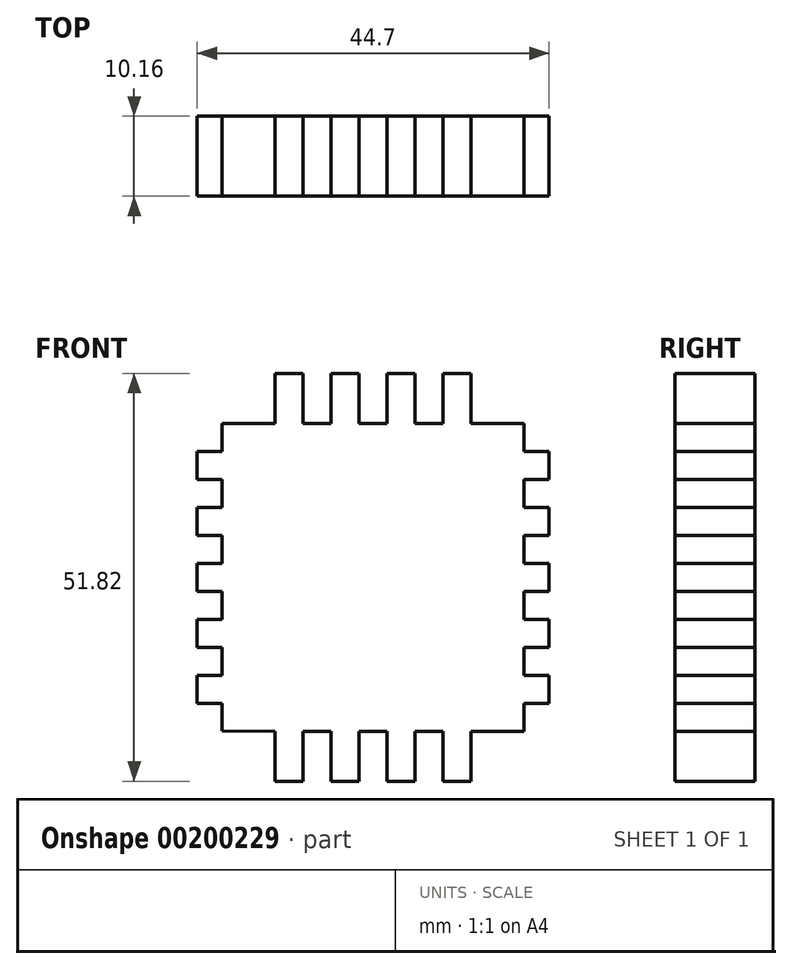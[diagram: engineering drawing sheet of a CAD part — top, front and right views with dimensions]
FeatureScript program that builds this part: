
annotation { "Feature Type Name" : "Feature", "Feature Type Description" : "" }
export const myFeature = defineFeature(function(context is Context, id is Id, definition is map)
    precondition{}
    {
        {
            var Q0;
            Q0=qCreatedBy(makeId("Front.planeOp"),FACE);
            var sketch = newSketch(context, id + "F0", { "sketchPlane" : qUnion([Q0])});
            skLineSegment(sketch, "E0", {"start": v(-12.15, -20.04) * mm, "end": v(-12.15, -26.39) * mm});
            skLineSegment(sketch, "E1", {"start": v(-12.15, -26.39) * mm, "end": v(-8.6, -26.39) * mm});
            skLineSegment(sketch, "E2", {"start": v(-8.6, -26.39) * mm, "end": v(-8.6, -20.04) * mm});
            skLineSegment(sketch, "E3", {"start": v(-8.6, -20.04) * mm, "end": v(-5.04, -20.04) * mm});
            skLineSegment(sketch, "E4", {"start": v(-5.04, -20.04) * mm, "end": v(-5.04, -26.39) * mm});
            skLineSegment(sketch, "E5", {"start": v(-5.04, -26.39) * mm, "end": v(-1.49, -26.39) * mm});
            skLineSegment(sketch, "E6", {"start": v(-1.49, -26.39) * mm, "end": v(-1.49, -20.04) * mm});
            skLineSegment(sketch, "E7", {"start": v(-1.49, -20.04) * mm, "end": v(2.07, -20.04) * mm});
            skLineSegment(sketch, "E8", {"start": v(2.07, -20.04) * mm, "end": v(2.07, -26.39) * mm});
            skLineSegment(sketch, "E9", {"start": v(2.07, -26.39) * mm, "end": v(5.63, -26.39) * mm});
            skLineSegment(sketch, "E10", {"start": v(5.63, -26.39) * mm, "end": v(5.63, -20.04) * mm});
            skLineSegment(sketch, "E11", {"start": v(5.63, -20.04) * mm, "end": v(9.18, -20.04) * mm});
            skLineSegment(sketch, "E12", {"start": v(9.18, -20.04) * mm, "end": v(9.18, -26.39) * mm});
            skLineSegment(sketch, "E13", {"start": v(9.18, -26.39) * mm, "end": v(12.74, -26.39) * mm});
            skLineSegment(sketch, "E14", {"start": v(12.74, -26.39) * mm, "end": v(12.74, -20.04) * mm});
            skLineSegment(sketch, "E15", {"start": v(22.64, -16.48) * mm, "end": v(22.64, -12.93) * mm});
            skLineSegment(sketch, "E16", {"start": v(22.64, -9.37) * mm, "end": v(22.64, -5.82) * mm});
            skLineSegment(sketch, "E17", {"start": v(22.64, -2.26) * mm, "end": v(22.64, 1.3) * mm});
            skLineSegment(sketch, "E18", {"start": v(22.64, 4.85) * mm, "end": v(22.64, 8.4) * mm});
            skLineSegment(sketch, "E19", {"start": v(22.64, 11.96) * mm, "end": v(22.64, 15.52) * mm});
            skLineSegment(sketch, "E20", {"start": v(12.74, 19.08) * mm, "end": v(12.74, 25.43) * mm});
            skLineSegment(sketch, "E21", {"start": v(12.74, 25.43) * mm, "end": v(9.18, 25.43) * mm});
            skLineSegment(sketch, "E22", {"start": v(9.18, 25.43) * mm, "end": v(9.18, 19.08) * mm});
            skLineSegment(sketch, "E23", {"start": v(9.18, 19.08) * mm, "end": v(5.63, 19.08) * mm});
            skLineSegment(sketch, "E24", {"start": v(5.63, 19.08) * mm, "end": v(5.63, 25.43) * mm});
            skLineSegment(sketch, "E25", {"start": v(5.63, 25.43) * mm, "end": v(2.07, 25.43) * mm});
            skLineSegment(sketch, "E26", {"start": v(2.07, 25.43) * mm, "end": v(2.07, 19.08) * mm});
            skLineSegment(sketch, "E27", {"start": v(2.07, 19.08) * mm, "end": v(-1.49, 19.08) * mm});
            skLineSegment(sketch, "E28", {"start": v(-1.49, 19.08) * mm, "end": v(-1.49, 25.43) * mm});
            skLineSegment(sketch, "E29", {"start": v(-1.49, 25.43) * mm, "end": v(-5.04, 25.43) * mm});
            skLineSegment(sketch, "E30", {"start": v(-5.04, 25.43) * mm, "end": v(-5.04, 19.08) * mm});
            skLineSegment(sketch, "E31", {"start": v(-5.04, 19.08) * mm, "end": v(-8.6, 19.08) * mm});
            skLineSegment(sketch, "E32", {"start": v(-8.6, 19.08) * mm, "end": v(-8.6, 25.43) * mm});
            skLineSegment(sketch, "E33", {"start": v(-8.6, 25.43) * mm, "end": v(-12.15, 25.43) * mm});
            skLineSegment(sketch, "E34", {"start": v(-12.15, 25.43) * mm, "end": v(-12.15, 19.08) * mm});
            skLineSegment(sketch, "E35", {"start": v(-22.06, -16.48) * mm, "end": v(-22.06, -12.93) * mm});
            skLineSegment(sketch, "E36", {"start": v(-22.06, -9.37) * mm, "end": v(-22.06, -5.82) * mm});
            skLineSegment(sketch, "E37", {"start": v(-22.06, -2.26) * mm, "end": v(-22.06, 1.3) * mm});
            skLineSegment(sketch, "E38", {"start": v(-22.06, 4.85) * mm, "end": v(-22.06, 8.4) * mm});
            skLineSegment(sketch, "E39", {"start": v(-22.06, 11.96) * mm, "end": v(-22.06, 15.52) * mm});
            skPoint(sketch, "E40.firstSnap0", {"position": v(-18.89, 15.52) * mm});
            skPoint(sketch, "E41.oppositeSnap0", {"position": v(19.47, -12.93) * mm});
            skLineSegment(sketch, "E42", {"start": v(22.64, 15.52) * mm, "end": v(19.47, 15.52) * mm});
            skLineSegment(sketch, "E43", {"start": v(22.64, 11.96) * mm, "end": v(19.47, 11.96) * mm});
            skLineSegment(sketch, "E44", {"start": v(22.64, 8.4) * mm, "end": v(19.47, 8.4) * mm});
            skLineSegment(sketch, "E45", {"start": v(22.64, 4.85) * mm, "end": v(19.47, 4.85) * mm});
            skLineSegment(sketch, "E46", {"start": v(22.64, -16.48) * mm, "end": v(19.47, -16.48) * mm});
            skLineSegment(sketch, "E47", {"start": v(22.64, -12.93) * mm, "end": v(19.47, -12.93) * mm});
            skLineSegment(sketch, "E48", {"start": v(22.64, -9.37) * mm, "end": v(19.47, -9.37) * mm});
            skLineSegment(sketch, "E49", {"start": v(22.64, -5.82) * mm, "end": v(19.47, -5.82) * mm});
            skLineSegment(sketch, "E50", {"start": v(22.64, -2.26) * mm, "end": v(19.47, -2.26) * mm});
            skLineSegment(sketch, "E51", {"start": v(22.64, 1.3) * mm, "end": v(19.47, 1.3) * mm});
            skLineSegment(sketch, "E52", {"start": v(19.47, 19.08) * mm, "end": v(19.47, 15.52) * mm});
            skLineSegment(sketch, "E53", {"start": v(19.47, 11.96) * mm, "end": v(19.47, 8.4) * mm});
            skLineSegment(sketch, "E54", {"start": v(19.47, 4.85) * mm, "end": v(19.47, 1.3) * mm});
            skLineSegment(sketch, "E55", {"start": v(19.47, -2.26) * mm, "end": v(19.47, -5.82) * mm});
            skLineSegment(sketch, "E56", {"start": v(19.47, -9.37) * mm, "end": v(19.47, -12.93) * mm});
            skLineSegment(sketch, "E57", {"start": v(19.47, -16.48) * mm, "end": v(19.47, -20.04) * mm});
            skLineSegment(sketch, "E58", {"start": v(-22.06, 15.52) * mm, "end": v(-18.89, 15.52) * mm});
            skLineSegment(sketch, "E59", {"start": v(-22.06, 11.96) * mm, "end": v(-18.89, 11.96) * mm});
            skLineSegment(sketch, "E60", {"start": v(-18.89, 11.96) * mm, "end": v(-18.89, 8.4) * mm});
            skLineSegment(sketch, "E61", {"start": v(-18.89, 8.4) * mm, "end": v(-22.06, 8.4) * mm});
            skLineSegment(sketch, "E62", {"start": v(-22.06, 4.85) * mm, "end": v(-18.89, 4.85) * mm});
            skLineSegment(sketch, "E63", {"start": v(-18.89, 4.85) * mm, "end": v(-18.89, 1.3) * mm});
            skLineSegment(sketch, "E64", {"start": v(-18.89, 1.3) * mm, "end": v(-22.06, 1.3) * mm});
            skLineSegment(sketch, "E65", {"start": v(-22.06, -2.26) * mm, "end": v(-18.89, -2.26) * mm});
            skLineSegment(sketch, "E66", {"start": v(-18.89, -2.26) * mm, "end": v(-18.89, -5.82) * mm});
            skLineSegment(sketch, "E67", {"start": v(-18.89, -5.82) * mm, "end": v(-22.06, -5.82) * mm});
            skLineSegment(sketch, "E68", {"start": v(-22.06, -9.37) * mm, "end": v(-18.89, -9.37) * mm});
            skLineSegment(sketch, "E69", {"start": v(-18.89, -9.37) * mm, "end": v(-18.89, -12.93) * mm});
            skLineSegment(sketch, "E70", {"start": v(-18.89, -12.93) * mm, "end": v(-22.06, -12.93) * mm});
            skLineSegment(sketch, "E71", {"start": v(-22.06, -16.48) * mm, "end": v(-18.89, -16.48) * mm});
            skLineSegment(sketch, "E72", {"start": v(-18.89, 19.08) * mm, "end": v(-18.89, 15.52) * mm});
            skLineSegment(sketch, "E73", {"start": v(-18.89, -16.48) * mm, "end": v(-18.89, -20) * mm});
            skLineSegment(sketch, "E74", {"start": v(12.74, 19.08) * mm, "end": v(19.47, 19.08) * mm});
            skLineSegment(sketch, "E75", {"start": v(19.47, -20.04) * mm, "end": v(12.74, -20.04) * mm});
            skLineSegment(sketch, "E76", {"start": v(-12.15, -20.04) * mm, "end": v(-18.89, -20) * mm});
            skLineSegment(sketch, "E77", {"start": v(-12.15, 19.08) * mm, "end": v(-18.89, 19.08) * mm});
            skSolve(sketch);
        }
        {
            var Q0;
            Q0=makeQuery(id+"F0.imprint","IMPRINT",FACE,{"disambiguationData":[TD([[makeQuery(id+"F0.imprint","IMPRINT",EDGE,{"derivedFrom":sQuery(id+"F0.wireOp",EDGE,"E0")}),1.0]])]});
            extrude(context, id + "F1", {"entities" : qUnion([Q0]), "depth" : 10.16 * mm});
        }
    });
